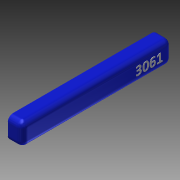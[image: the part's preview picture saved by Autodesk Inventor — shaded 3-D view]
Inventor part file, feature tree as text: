
AUTODESK INVENTOR PART (.ipt)
format: ipt  version: 2013 (Build 170138000, 138)  size: 361,984 bytes
history: native  units: in
note: dims shown in document units (in); Inventor stores cm internally (conversion verified against a paired STEP export)
features: reference x7, extrude x4, sketch x3, fillet x1, projected_geometry x1
ambient origin geometry x8: Origin, YZ Plane, XZ Plane, XY Plane, X Axis, Y Axis, Z Axis, Center Point
bodies: Solid1 (feature_tree)
feature tree (16):
  sketch  "Sketch1"  dims[d0=0.0625in d1=0.0in d3=1.0in]
  extrude  "Extrusion1"  Depth=1.0in
  extrude  "Extrusion2"  Depth=0.0625in
  extrude  "Extrusion3"  Depth=0.0625in TaperAngle=0.0deg
  fillet  "Fillet1"  Radius=1.3125in
  extrude  "Extrusion5"  Depth=0.0625in
  reference  "Reference4"
  reference  "Reference5"
  sketch  "Sketch2"  dims[d7=1.0in d9=0.0625in]
  reference  "Reference6"
  reference  "Reference7"
  reference  "Reference8"
  reference  "Reference9"
  reference  "Reference10"
  projected_geometry  "Projected Loop1"
  sketch  "Sketch4"  dims[d10=34.5in d11=0.0in d12=0.0625in d13=0.0in d14=1.3125in d20=0.0625in d21=0.0625in d26=1.0in d27=6.0in d28=2.5in d29=0.0625in d30=0.0in]
